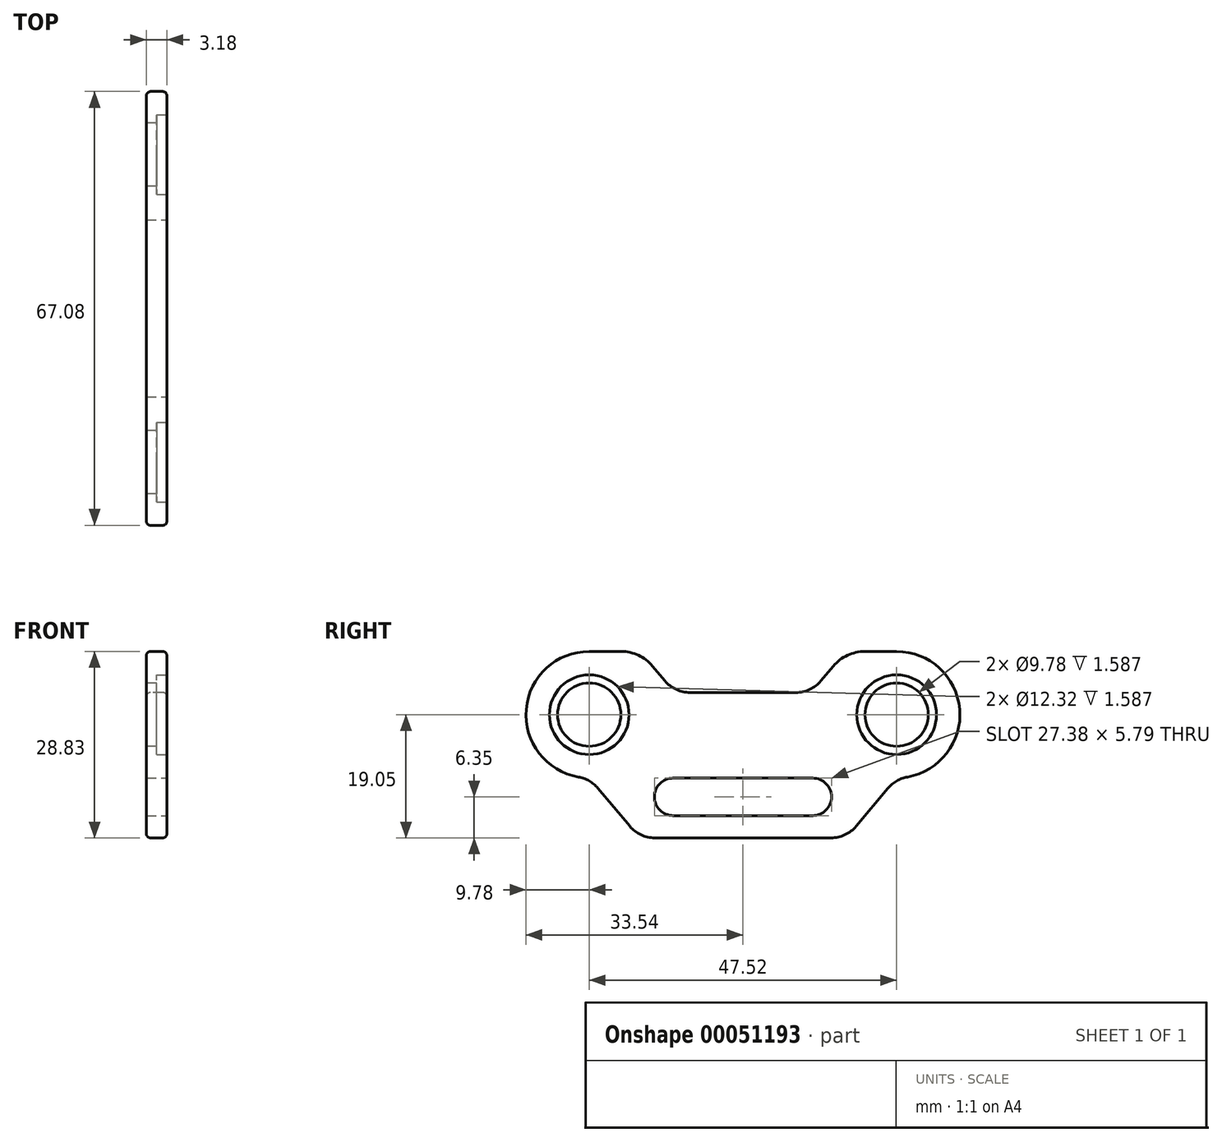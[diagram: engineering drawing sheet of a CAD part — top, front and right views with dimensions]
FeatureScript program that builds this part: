
annotation { "Feature Type Name" : "Feature", "Feature Type Description" : "" }
export const myFeature = defineFeature(function(context is Context, id is Id, definition is map)
    precondition{}
    {
        {
            var Q0;
            Q0=qCreatedBy(makeId("Right.planeOp"),FACE);
            var sketch = newSketch(context, id + "F0", { "sketchPlane" : qUnion([Q0])});
            skLineSegment(sketch, "E0", {"start": v(-23.76, 0) * mm, "end": v(23.76, 0) * mm, "construction": true});
            skCircle(sketch, "E1", {"center": v(-23.76, 0) * mm, "radius": 4.89 * mm});
            skCircle(sketch, "E2", {"center": v(23.76, 0) * mm, "radius": 4.89 * mm});
            skArc(sketch, "E3", {"start": v(23.76, -9.78) * mm, "mid": v(33.54, 0) * mm, "end": v(23.76, 9.78) * mm});
            skArc(sketch, "E4", {"start": v(-23.76, 9.78) * mm, "mid": v(-33.54, 0) * mm, "end": v(-23.76, -9.78) * mm});
            skLineSegment(sketch, "E5", {"start": v(-23.76, 9.78) * mm, "end": v(-15.88, 9.78) * mm});
            skLineSegment(sketch, "E6", {"start": v(-15.98, -19.05) * mm, "end": v(15.98, -19.05) * mm});
            skLineSegment(sketch, "E7", {"start": v(15.98, -19.05) * mm, "end": v(23.76, -9.78) * mm});
            skLineSegment(sketch, "E8", {"start": v(0, 0) * mm, "end": v(0, -19.05) * mm, "construction": true});
            skLineSegment(sketch, "E9", {"start": v(-23.76, 0) * mm, "end": v(-23.76, -9.78) * mm, "construction": true});
            skLineSegment(sketch, "E10", {"start": v(23.76, 0) * mm, "end": v(23.76, -9.78) * mm, "construction": true});
            skLineSegment(sketch, "E11", {"start": v(-23.76, 0) * mm, "end": v(-23.76, 9.78) * mm, "construction": true});
            skLineSegment(sketch, "E12", {"start": v(23.76, 0) * mm, "end": v(23.76, 9.78) * mm, "construction": true});
            skLineSegment(sketch, "E13", {"start": v(-23.76, -9.78) * mm, "end": v(-15.98, -19.05) * mm});
            skLineSegment(sketch, "E14", {"start": v(-15.88, 9.78) * mm, "end": v(-10.55, 3.43) * mm});
            skLineSegment(sketch, "E15", {"start": v(-10.55, 3.43) * mm, "end": v(10.55, 3.43) * mm});
            skLineSegment(sketch, "E16", {"start": v(10.55, 3.43) * mm, "end": v(15.88, 9.78) * mm});
            skLineSegment(sketch, "E17", {"start": v(0, 0) * mm, "end": v(0, 3.43) * mm, "construction": true});
            skLineSegment(sketch, "E18.trimOffspring", {"start": v(15.88, 9.78) * mm, "end": v(23.76, 9.78) * mm});
            skSolve(sketch);
        }
        {
            var Q0;
            Q0=makeQuery(id+"F0.imprint","IMPRINT",FACE,{"disambiguationData":[TD([[makeQuery(id+"F0.imprint","IMPRINT",EDGE,{"derivedFrom":sQuery(id+"F0.wireOp",EDGE,"E1")}),-1.0]])]});
            extrude(context, id + "F1", {"entities" : qUnion([Q0]), "endBound" : BoundingType.SYMMETRIC, "depth" : 3.17 * mm});
        }
        {
            var Q0;
            Q0=makeQuery(id+"F1.opExtrude","SWEPT_EDGE",EDGE,{"disambiguationData":[OSD([sQuery(id+"F0.wireOp",EDGE,"E6"),sQuery(id+"F0.wireOp",EDGE,"E13")])]});
            var Q1;
            Q1=makeQuery(id+"F1.opExtrude","SWEPT_EDGE",EDGE,{"disambiguationData":[OSD([sQuery(id+"F0.wireOp",EDGE,"E6"),sQuery(id+"F0.wireOp",EDGE,"E7")])]});
            fillet(context, id + "F2", {"entities" : qUnion([Q0, Q1]), "radius" : 5.08 * mm, "tangentPropagation" : true, "allowEdgeOverflow" : false});
        }
        {
            var Q0;
            Q0=makeQuery(id+"F1.opExtrude","SWEPT_EDGE",EDGE,{"disambiguationData":[OSD([sQuery(id+"F0.wireOp",EDGE,"E14"),sQuery(id+"F0.wireOp",EDGE,"E15")])]});
            var Q1;
            Q1=makeQuery(id+"F1.opExtrude","SWEPT_EDGE",EDGE,{"disambiguationData":[OSD([sQuery(id+"F0.wireOp",EDGE,"E15"),sQuery(id+"F0.wireOp",EDGE,"E16")])]});
            fillet(context, id + "F3", {"entities" : qUnion([Q0, Q1]), "radius" : 5.08 * mm, "tangentPropagation" : true, "allowEdgeOverflow" : false});
        }
        {
            var Q0;
            Q0=makeQuery(id+"F1.opExtrude","SWEPT_EDGE",EDGE,{"disambiguationData":[OSD([sQuery(id+"F0.wireOp",EDGE,"E5"),sQuery(id+"F0.wireOp",EDGE,"E14")])]});
            var Q1;
            Q1=makeQuery(id+"F1.opExtrude","SWEPT_EDGE",EDGE,{"disambiguationData":[OSD([sQuery(id+"F0.wireOp",EDGE,"E16"),sQuery(id+"F0.wireOp",EDGE,"E18.trimOffspring")])]});
            fillet(context, id + "F4", {"entities" : qUnion([Q0, Q1]), "radius" : 6.35 * mm, "tangentPropagation" : true, "allowEdgeOverflow" : false});
        }
        {
            var Q0;
            Q0=makeQuery(id+"F1.opExtrude","SWEPT_EDGE",EDGE,{"disambiguationData":[OSD([sQuery(id+"F0.wireOp",EDGE,"E4"),sQuery(id+"F0.wireOp",EDGE,"E13")])]});
            var Q1;
            Q1=makeQuery(id+"F1.opExtrude","SWEPT_EDGE",EDGE,{"disambiguationData":[OSD([sQuery(id+"F0.wireOp",EDGE,"E3"),sQuery(id+"F0.wireOp",EDGE,"E7")])]});
            fillet(context, id + "F5", {"entities" : qUnion([Q0, Q1]), "radius" : 5.08 * mm, "tangentPropagation" : true, "allowEdgeOverflow" : false});
        }
        {
            var Q0;
            Q0=qCreatedBy(makeId("Right.planeOp"),FACE);
            var sketch = newSketch(context, id + "F6", { "sketchPlane" : qUnion([Q0])});
            skLineSegment(sketch, "E19", {"start": v(-10.8, -12.7) * mm, "end": v(10.8, -12.7) * mm, "construction": true});
            skLineSegment(sketch, "E20", {"start": v(0, 0) * mm, "end": v(0, -12.7) * mm, "construction": true});
            skArc(sketch, "E21", {"start": v(-10.8, -9.8) * mm, "mid": v(-13.7, -12.7) * mm, "end": v(-10.8, -15.6) * mm});
            skArc(sketch, "E22", {"start": v(10.8, -15.6) * mm, "mid": v(13.7, -12.7) * mm, "end": v(10.8, -9.8) * mm});
            skLineSegment(sketch, "E23", {"start": v(-10.8, -9.8) * mm, "end": v(10.8, -9.8) * mm});
            skLineSegment(sketch, "E24", {"start": v(10.8, -15.6) * mm, "end": v(-10.8, -15.6) * mm});
            skSolve(sketch);
        }
        {
            var Q0;
            Q0 = qSketchRegion(id + "F6", true);
            extrude(context, id + "F7", {"entities" : qUnion([Q0]), "operationType" : NewBodyOperationType.REMOVE, "endBound" : BoundingType.SYMMETRIC, "oppositeDirection" : true, "depth" : 25.4 * mm});
        }
        {
            var Q0;
            Q0=makeQuery(id+"F1.opExtrude","CAP_FACE",FACE,{"disambiguationData":[OSD([sQuery(id+"F0.wireOp",EDGE,"E1"),sQuery(id+"F0.wireOp",EDGE,"E2"),sQuery(id+"F0.wireOp",EDGE,"E3"),sQuery(id+"F0.wireOp",EDGE,"E4"),sQuery(id+"F0.wireOp",EDGE,"E5"),sQuery(id+"F0.wireOp",EDGE,"E6"),sQuery(id+"F0.wireOp",EDGE,"E7"),sQuery(id+"F0.wireOp",EDGE,"E13"),sQuery(id+"F0.wireOp",EDGE,"E14"),sQuery(id+"F0.wireOp",EDGE,"E15"),sQuery(id+"F0.wireOp",EDGE,"E16"),sQuery(id+"F0.wireOp",EDGE,"E18.trimOffspring")])],"isStart":false});
            var sketch = newSketch(context, id + "F8", { "sketchPlane" : qUnion([Q0])});
            skCircle(sketch, "E25", {"center": v(-23.76, 0) * mm, "radius": 6.16 * mm});
            skCircle(sketch, "E26", {"center": v(23.76, 0) * mm, "radius": 6.16 * mm});
            skSolve(sketch);
        }
        {
            var Q0;
            Q0 = qSketchRegion(id + "F8", true);
            extrude(context, id + "F9", {"entities" : qUnion([Q0]), "operationType" : NewBodyOperationType.REMOVE, "oppositeDirection" : true, "depth" : 1.59 * mm});
        }
        {
            var Q0;
            Q0=makeQuery(id+"F1.opExtrude","CAP_EDGE",EDGE,{"disambiguationData":[OSD([sQuery(id+"F0.wireOp",EDGE,"E13")])],"isStart":false});
            var Q1;
            Q1=makeQuery(id+"F1.opExtrude","CAP_EDGE",EDGE,{"disambiguationData":[OSD([sQuery(id+"F0.wireOp",EDGE,"E4")])],"isStart":true});
            fillet(context, id + "F10", {"entities" : qUnion([Q0, Q1]), "radius" : 0.64 * mm, "tangentPropagation" : true, "allowEdgeOverflow" : false});
        }
    });
